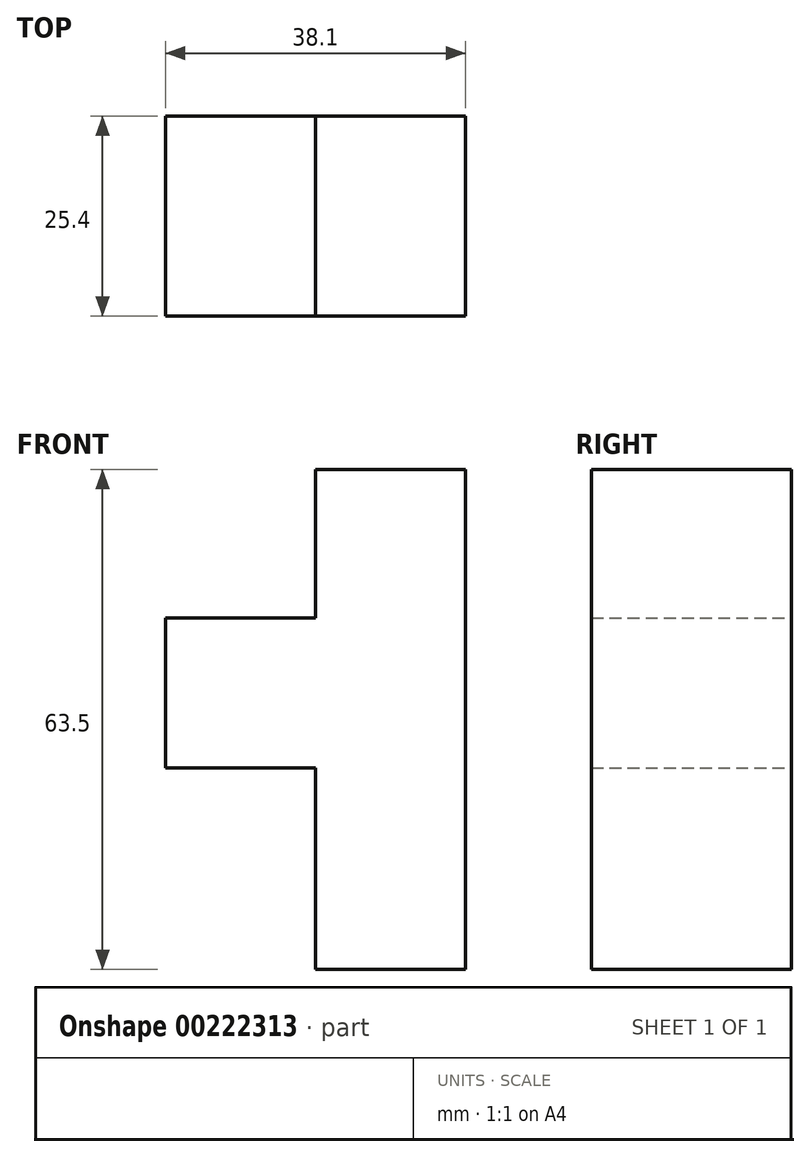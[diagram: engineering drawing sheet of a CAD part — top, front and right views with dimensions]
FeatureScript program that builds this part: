
annotation { "Feature Type Name" : "Feature", "Feature Type Description" : "" }
export const myFeature = defineFeature(function(context is Context, id is Id, definition is map)
    precondition{}
    {
        {
            var Q0;
            Q0=qCreatedBy(makeId("Front.planeOp"),FACE);
            var sketch = newSketch(context, id + "F0", { "sketchPlane" : qUnion([Q0])});
            skLineSegment(sketch, "E0.bottom", {"start": v(-22.76, -6.2) * mm, "end": v(-41.81, -6.2) * mm});
            skLineSegment(sketch, "E0.top", {"start": v(-22.76, 57.3) * mm, "end": v(-41.81, 57.3) * mm});
            skLineSegment(sketch, "E0.left", {"start": v(-22.76, -6.2) * mm, "end": v(-22.76, 57.3) * mm});
            skLineSegment(sketch, "E0.right", {"start": v(-41.81, -6.2) * mm, "end": v(-41.81, 57.3) * mm});
            skPoint(sketch, "E0.middle", {"position": v(-32.29, 25.55) * mm});
            skLineSegment(sketch, "E1.bottom", {"start": v(-41.81, 19.4) * mm, "end": v(-60.86, 19.4) * mm});
            skLineSegment(sketch, "E1.top", {"start": v(-41.81, 38.45) * mm, "end": v(-60.86, 38.45) * mm});
            skLineSegment(sketch, "E1.left", {"start": v(-41.81, 19.4) * mm, "end": v(-41.81, 38.45) * mm});
            skLineSegment(sketch, "E1.right", {"start": v(-60.86, 19.4) * mm, "end": v(-60.86, 38.45) * mm});
            skPoint(sketch, "E1.middle", {"position": v(-51.34, 28.93) * mm});
            skSolve(sketch);
        }
        {
            var Q0;
            Q0=qSketchRegion(id+"F0",true);
            extrude(context, id + "F1", {"entities" : qUnion([Q0]), "endBound" : BoundingType.SYMMETRIC, "depth" : 25.4 * mm});
        }
    });
